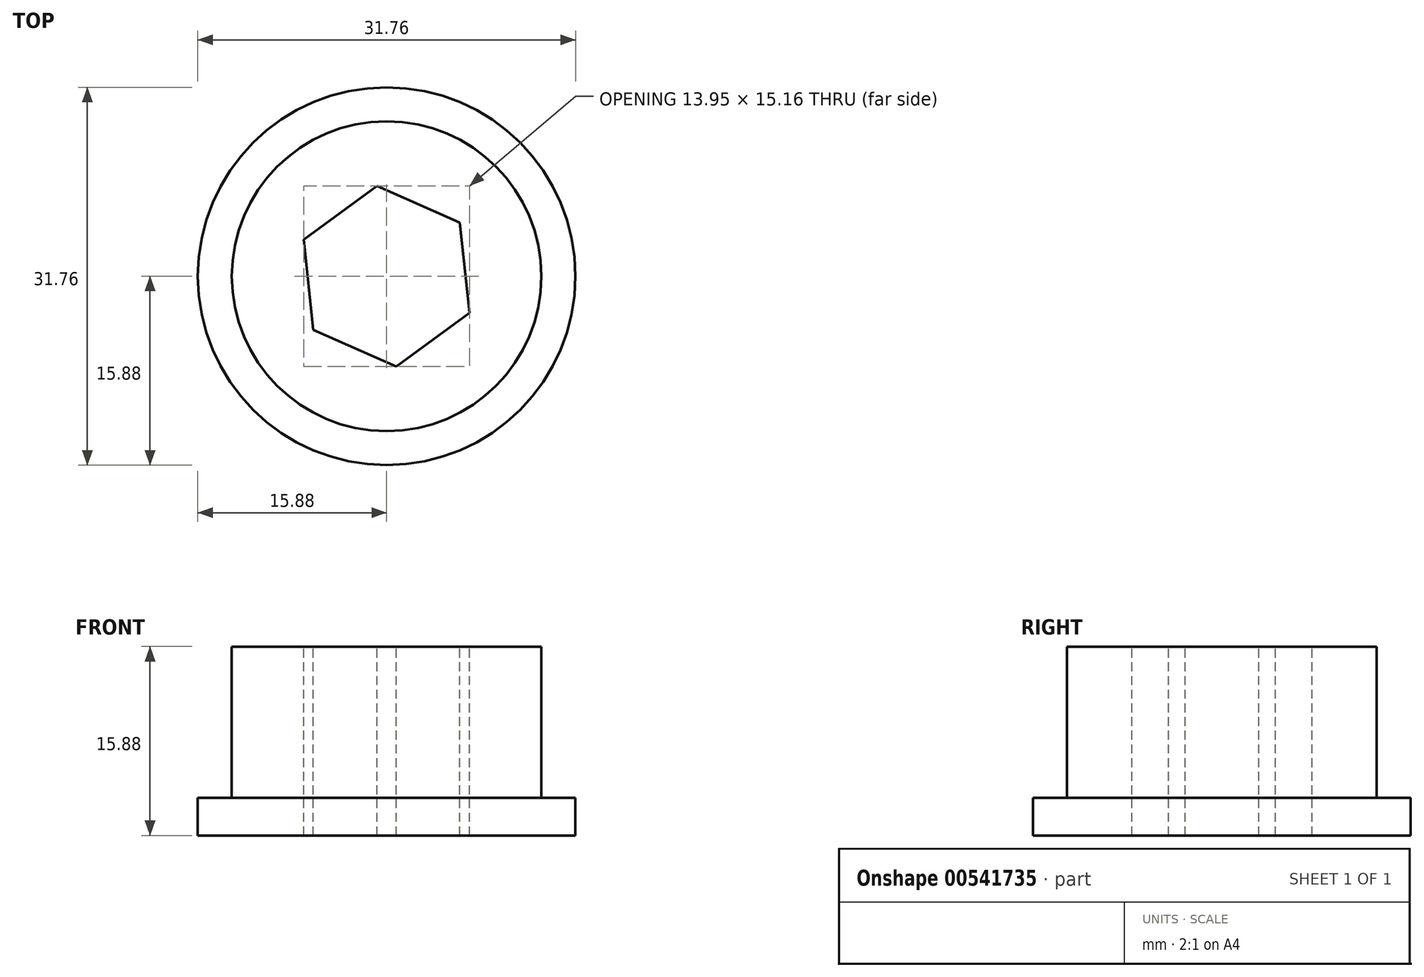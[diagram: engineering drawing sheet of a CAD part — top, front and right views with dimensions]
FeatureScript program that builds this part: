
annotation { "Feature Type Name" : "Feature", "Feature Type Description" : "" }
export const myFeature = defineFeature(function(context is Context, id is Id, definition is map)
    precondition{}
    {
        {
            var Q0;
            Q0=qCreatedBy(makeId("Top.planeOp"),FACE);
            var sketch = newSketch(context, id + "F0", { "sketchPlane" : qUnion([Q0])});
            skCircle(sketch, "E0", {"center": v(0, 0) * mm, "radius": 15.88 * mm});
            skSolve(sketch);
        }
        {
            var Q0;
            Q0 = qSketchRegion(id + "F0", true);
            extrude(context, id + "F1", {"entities" : qUnion([Q0]), "depth" : 3.17 * mm, "offsetDistance" : 25.4 * mm});
        }
        {
            var Q0;
            Q0=makeQuery(id+"F1.opExtrude","CAP_FACE",FACE,{"disambiguationData":[OSD([sQuery(id+"F0.wireOp",EDGE,"E0")])],"isStart":false});
            var sketch = newSketch(context, id + "F2", { "sketchPlane" : qUnion([Q0])});
            skCircle(sketch, "E1", {"center": v(0, 0) * mm, "radius": 13.02 * mm});
            skSolve(sketch);
        }
        {
            var Q0;
            Q0 = qSketchRegion(id + "F2", true);
            extrude(context, id + "F3", {"entities" : qUnion([Q0]), "operationType" : NewBodyOperationType.ADD, "depth" : 12.7 * mm, "offsetDistance" : 25.4 * mm});
        }
        {
            var Q0;
            Q0=makeQuery(id+"F3.opExtrude","CAP_FACE",FACE,{"disambiguationData":[OSD([sQuery(id+"F2.wireOp",EDGE,"E1")])],"isStart":false});
            var sketch = newSketch(context, id + "F4", { "sketchPlane" : qUnion([Q0])});
            skCircle(sketch, "E2.cCircle", {"center": v(0, 0) * mm, "radius": 6.6 * mm, "construction": true});
            skLineSegment(sketch, "E2.0", {"start": v(-0.81, 7.58) * mm, "end": v(6.16, 4.5) * mm});
            skLineSegment(sketch, "E2.1", {"start": v(6.16, 4.5) * mm, "end": v(6.97, -3.09) * mm});
            skLineSegment(sketch, "E2.2", {"start": v(6.97, -3.09) * mm, "end": v(0.81, -7.58) * mm});
            skLineSegment(sketch, "E2.3", {"start": v(0.81, -7.58) * mm, "end": v(-6.16, -4.5) * mm});
            skLineSegment(sketch, "E2.4", {"start": v(-6.16, -4.5) * mm, "end": v(-6.97, 3.09) * mm});
            skLineSegment(sketch, "E2.5", {"start": v(-6.97, 3.09) * mm, "end": v(-0.81, 7.58) * mm});
            skPoint(sketch, "E2.0.midPoint", {"position": v(2.67, 6.04) * mm});
            skSolve(sketch);
        }
        {
            var Q0;
            Q0=makeQuery(id+"F4.imprint","IMPRINT",FACE,{"disambiguationData":[TD([[makeQuery(id+"F4.imprint","IMPRINT",EDGE,{"derivedFrom":sQuery(id+"F4.wireOp",EDGE,"E2.0")}),-1.0]])]});
            extrude(context, id + "F5", {"entities" : qUnion([Q0]), "operationType" : NewBodyOperationType.REMOVE, "endBound" : BoundingType.THROUGH_ALL, "oppositeDirection" : true, "depth" : 25.4 * mm, "offsetDistance" : 25.4 * mm});
        }
    });
